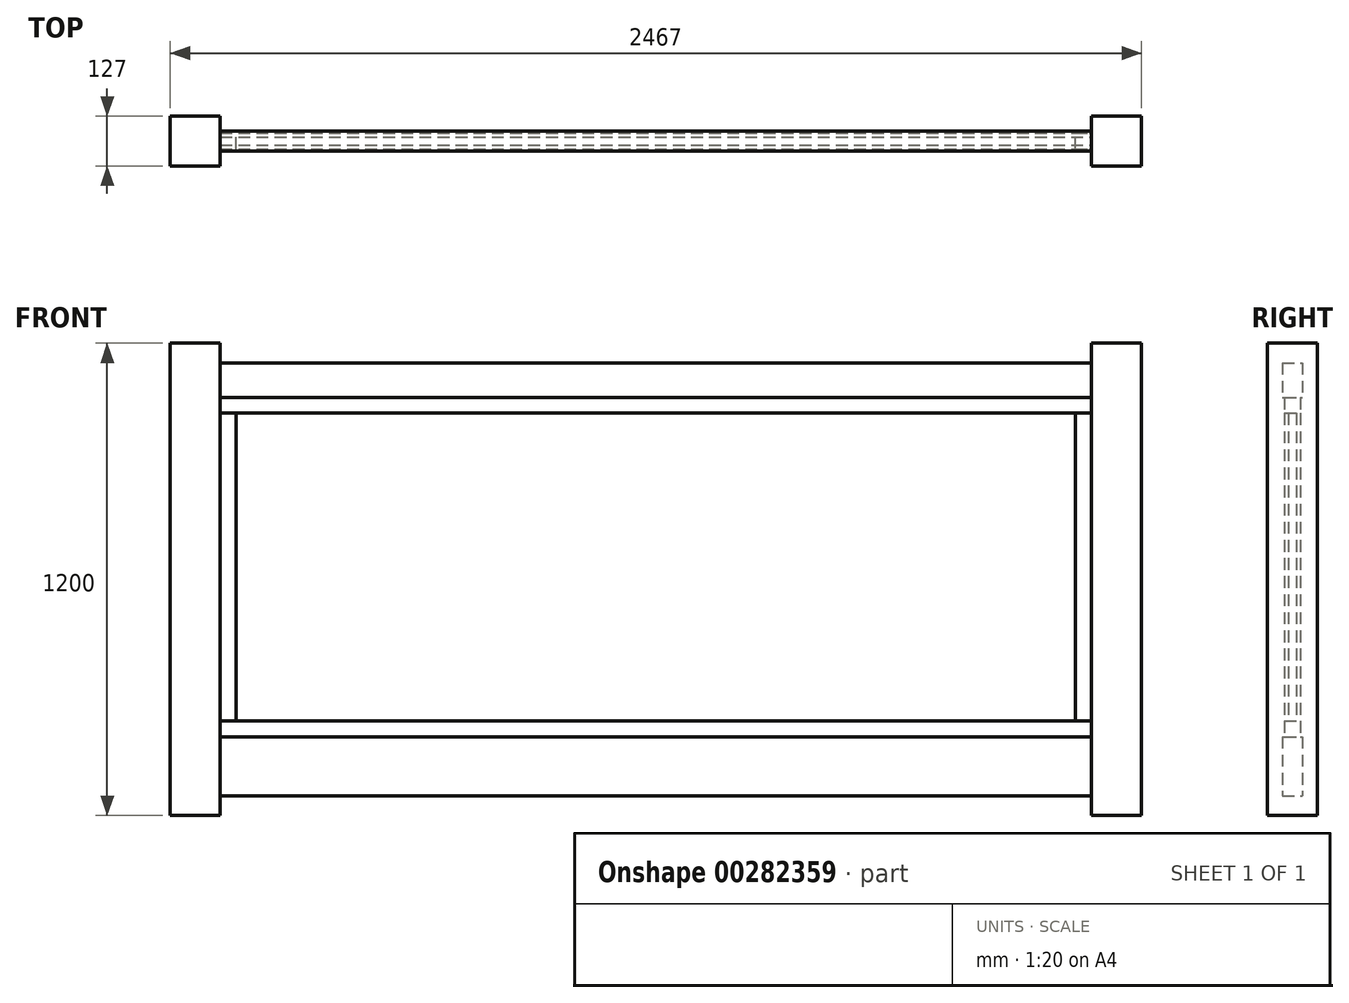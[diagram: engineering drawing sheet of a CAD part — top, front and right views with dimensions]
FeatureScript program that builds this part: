
annotation { "Feature Type Name" : "Feature", "Feature Type Description" : "" }
export const myFeature = defineFeature(function(context is Context, id is Id, definition is map)
    precondition{}
    {
        {
            var Q0;
            Q0=qCreatedBy(makeId("Front.planeOp"),FACE);
            var sketch = newSketch(context, id + "F0", { "sketchPlane" : qUnion([Q0])});
            skLineSegment(sketch, "E0.bottom", {"start": v(1233.5, -600) * mm, "end": v(1106.5, -600) * mm});
            skLineSegment(sketch, "E0.top", {"start": v(1233.5, 600) * mm, "end": v(1106.5, 600) * mm});
            skLineSegment(sketch, "E0.left", {"start": v(1233.5, -600) * mm, "end": v(1233.5, 600) * mm});
            skLineSegment(sketch, "E0.right", {"start": v(-1233.5, -600) * mm, "end": v(-1233.5, 600) * mm});
            skPoint(sketch, "E0.middle", {"position": v(0, 0) * mm});
            skLineSegment(sketch, "E1", {"start": v(-1106.5, 600) * mm, "end": v(-1106.5, -600) * mm});
            skLineSegment(sketch, "E2", {"start": v(1106.5, 600) * mm, "end": v(1106.5, -600) * mm});
            skLineSegment(sketch, "E3.trimOffspring", {"start": v(-1106.5, 600) * mm, "end": v(-1233.5, 600) * mm});
            skLineSegment(sketch, "E4", {"start": v(-1106.5, 550) * mm, "end": v(1106.5, 550) * mm});
            skLineSegment(sketch, "E5", {"start": v(-1106.5, 462) * mm, "end": v(1106.5, 462) * mm});
            skLineSegment(sketch, "E6", {"start": v(-1106.5, -550) * mm, "end": v(1106.5, -550) * mm});
            skLineSegment(sketch, "E7", {"start": v(-1106.5, -400) * mm, "end": v(1106.5, -400) * mm});
            skLineSegment(sketch, "E8.trimOffspring", {"start": v(-1106.5, -600) * mm, "end": v(-1233.5, -600) * mm});
            skLineSegment(sketch, "E9", {"start": v(-1106.5, -360) * mm, "end": v(1106.5, -360) * mm});
            skLineSegment(sketch, "E10", {"start": v(-1106.5, 422) * mm, "end": v(1106.5, 422) * mm});
            skLineSegment(sketch, "E11", {"start": v(-1066.5, 422) * mm, "end": v(-1066.5, -360) * mm});
            skLineSegment(sketch, "E12", {"start": v(1066.5, -360) * mm, "end": v(1066.5, 422) * mm});
            skSolve(sketch);
        }
        {
            var Q0;
            Q0=makeQuery(id+"F0.imprint","IMPRINT",FACE,{"disambiguationData":[TD([[makeQuery(id+"F0.imprint","IMPRINT",EDGE,{"derivedFrom":sQuery(id+"F0.wireOp",EDGE,"E0.right")}),-1.0]])]});
            var Q1;
            {var subQ8=sQuery(id+"F0.wireOp",EDGE,"E0.bottom");Q1=makeQuery(id+"F0.imprint","IMPRINT",FACE,{"disambiguationData":[TD([[makeQuery(id+"F0.imprint","IMPRINT",EDGE,{"derivedFrom":subQ8}),-1.0]])]});}
            extrude(context, id + "F1", {"entities" : qUnion([Q0, Q1]), "depth" : 63.5 * mm, "hasSecondDirection" : true, "secondDirectionOppositeDirection" : true, "secondDirectionDepth" : 63.5 * mm});
        }
        {
            var Q0;
            {var subQ0=sQuery(id+"F0.wireOp",EDGE,"E6");Q0=makeQuery(id+"F0.imprint","IMPRINT",FACE,{"disambiguationData":[TD([[makeQuery(id+"F0.imprint","IMPRINT",EDGE,{"derivedFrom":subQ0}),1.0]])]});}
            var Q1;
            {var subQ0=sQuery(id+"F0.wireOp",EDGE,"yRPGKGca-anLp-XnGH-KkSi-gyNm5ic0emfk");Q1=makeQuery(id+"F0.imprint","IMPRINT",FACE,{"disambiguationData":[TD([[makeQuery(id+"F0.imprint","IMPRINT",EDGE,{"derivedFrom":subQ0}),-1.0]])]});}
            var Q2;
            {var subQ0=sQuery(id+"F0.wireOp",EDGE,"E4");Q2=makeQuery(id+"F0.imprint","IMPRINT",FACE,{"disambiguationData":[TD([[makeQuery(id+"F0.imprint","IMPRINT",EDGE,{"derivedFrom":subQ0}),-1.0]])]});}
            extrude(context, id + "F2", {"entities" : qUnion([Q0, Q1, Q2]), "depth" : 25 * mm, "hasSecondDirection" : true, "secondDirectionOppositeDirection" : true, "secondDirectionDepth" : 25 * mm});
        }
        {
            var Q0;
            {var subQ0=sQuery(id+"F0.wireOp",EDGE,"E5");Q0=makeQuery(id+"F0.imprint","IMPRINT",FACE,{"disambiguationData":[TD([[makeQuery(id+"F0.imprint","IMPRINT",EDGE,{"derivedFrom":subQ0}),-1.0]])]});}
            var Q1;
            {var subQ0=sQuery(id+"F0.wireOp",EDGE,"E7");Q1=makeQuery(id+"F0.imprint","IMPRINT",FACE,{"disambiguationData":[TD([[makeQuery(id+"F0.imprint","IMPRINT",EDGE,{"derivedFrom":subQ0}),1.0]])]});}
            extrude(context, id + "F3", {"entities" : qUnion([Q0, Q1]), "depth" : 20 * mm, "hasSecondDirection" : true, "secondDirectionOppositeDirection" : true, "secondDirectionDepth" : 20 * mm});
        }
        {
            var Q0;
            {var subQ0=sQuery(id+"F0.wireOp",EDGE,"E9");Q0=makeQuery(id+"F0.imprint","IMPRINT",FACE,{"disambiguationData":[TD([[makeQuery(id+"F0.imprint","IMPRINT",EDGE,{"derivedFrom":subQ0}),1.0]])]});}
            extrude(context, id + "F4", {"entities" : qUnion([Q0]), "depth" : 10 * mm, "hasSecondDirection" : true, "secondDirectionOppositeDirection" : true, "secondDirectionDepth" : 10 * mm});
        }
        {
            var Q0;
            {var subQ5=sQuery(id+"F0.wireOp",EDGE,"E11");Q0=makeQuery(id+"F0.imprint","IMPRINT",FACE,{"disambiguationData":[TD([[makeQuery(id+"F0.imprint","IMPRINT",EDGE,{"derivedFrom":subQ5}),-1.0]])]});}
            var Q1;
            {var subQ5=sQuery(id+"F0.wireOp",EDGE,"E12");Q1=makeQuery(id+"F0.imprint","IMPRINT",FACE,{"disambiguationData":[TD([[makeQuery(id+"F0.imprint","IMPRINT",EDGE,{"derivedFrom":subQ5}),-1.0]])]});}
            extrude(context, id + "F5", {"entities" : qUnion([Q0, Q1]), "depth" : 20 * mm, "hasSecondDirection" : true, "secondDirectionOppositeDirection" : true, "secondDirectionDepth" : 20 * mm});
        }
    });
